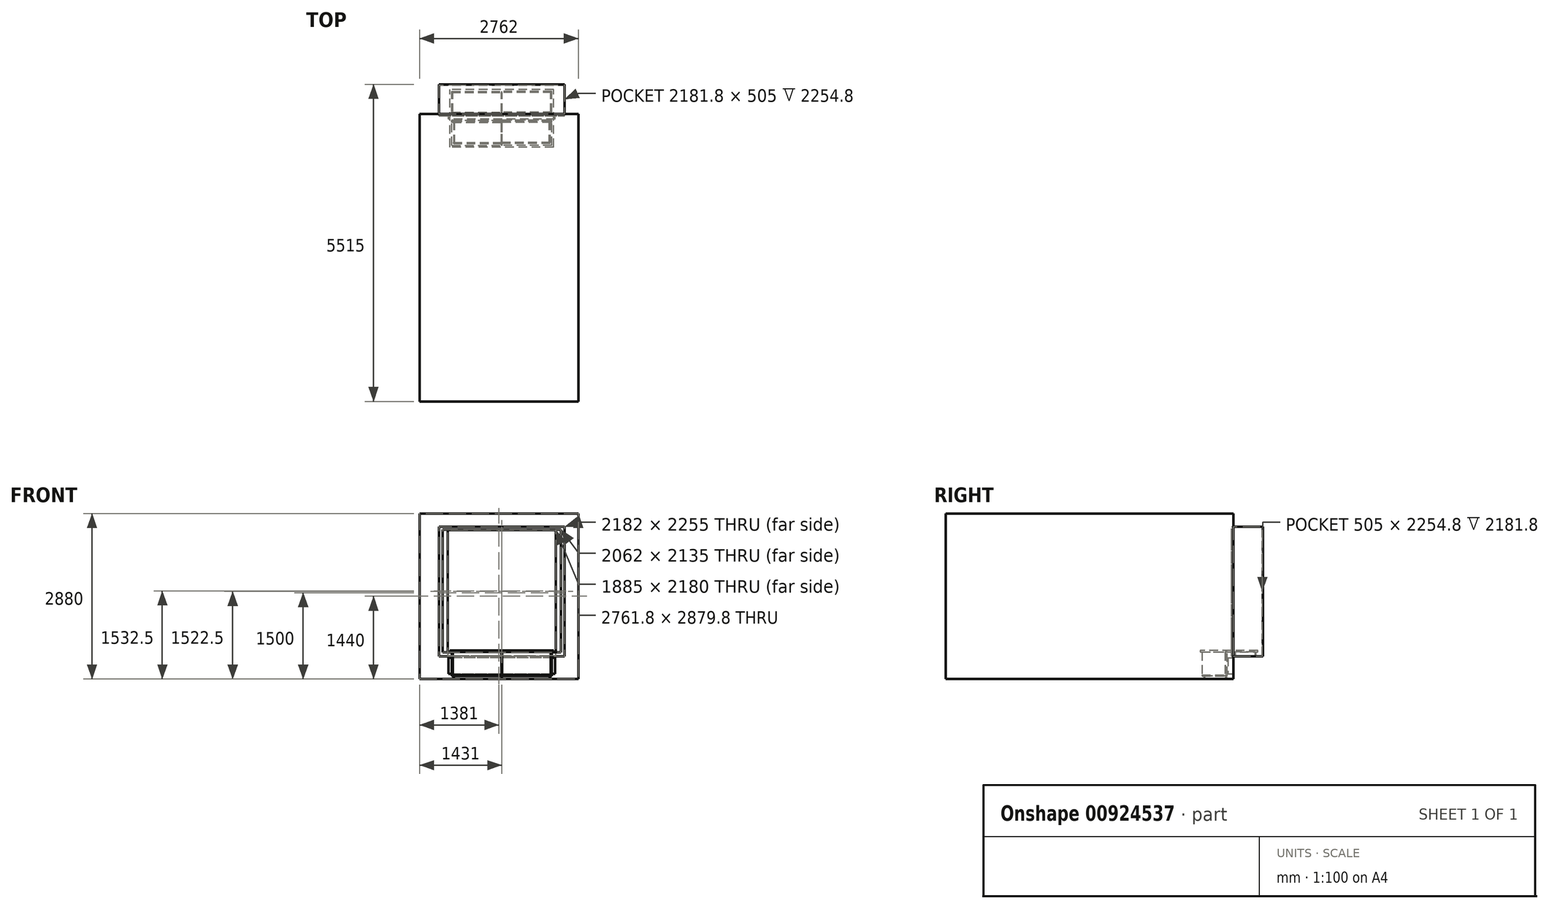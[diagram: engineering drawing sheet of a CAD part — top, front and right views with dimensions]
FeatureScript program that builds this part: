
annotation { "Feature Type Name" : "Feature", "Feature Type Description" : "" }
export const myFeature = defineFeature(function(context is Context, id is Id, definition is map)
    precondition{}
    {
        {
            var Q0;
            Q0=qCreatedBy(makeId("Front.planeOp"),FACE);
            var sketch = newSketch(context, id + "F0", { "sketchPlane" : qUnion([Q0])});
            skLineSegment(sketch, "E0", {"start": v(-1031, 0) * mm, "end": v(1031, 0) * mm});
            skPoint(sketch, "E1", {"position": v(0, 0) * mm});
            skLineSegment(sketch, "E2", {"start": v(-1031, 0) * mm, "end": v(-1031, 2135) * mm});
            skLineSegment(sketch, "E3", {"start": v(-1031, 2135) * mm, "end": v(1031, 2135) * mm});
            skLineSegment(sketch, "E4", {"start": v(1031, 2135) * mm, "end": v(1031, 0) * mm});
            skLineSegment(sketch, "E5", {"start": v(0, 0) * mm, "end": v(0, 2135) * mm, "construction": true});
            skLineSegment(sketch, "E6", {"start": v(-942.5, -55) * mm, "end": v(942.5, -55) * mm, "construction": true});
            skLineSegment(sketch, "E7", {"start": v(942.5, -55) * mm, "end": v(942.5, 2125) * mm, "construction": true});
            skLineSegment(sketch, "E8", {"start": v(942.5, 2125) * mm, "end": v(-942.5, 2125) * mm, "construction": true});
            skLineSegment(sketch, "E9", {"start": v(-942.5, 2125) * mm, "end": v(-942.5, -55) * mm, "construction": true});
            skPoint(sketch, "E10", {"position": v(0, -55) * mm});
            skLineSegment(sketch, "E11.0", {"start": v(-1091, -70) * mm, "end": v(-1091, 2185) * mm});
            skLineSegment(sketch, "E11.1", {"start": v(-1091, -70) * mm, "end": v(1091, -70) * mm});
            skLineSegment(sketch, "E11.2", {"start": v(1091, 2185) * mm, "end": v(1091, -70) * mm});
            skLineSegment(sketch, "E11.3", {"start": v(-1091, 2185) * mm, "end": v(1091, 2185) * mm});
            skPoint(sketch, "E12", {"position": v(0, -70) * mm});
            skLineSegment(sketch, "E13", {"start": v(-1431, -465) * mm, "end": v(-1431, 2415) * mm});
            skLineSegment(sketch, "E14", {"start": v(-1431, 2415) * mm, "end": v(1331, 2415) * mm});
            skLineSegment(sketch, "E15", {"start": v(1331, 2415) * mm, "end": v(1331, -465) * mm});
            skLineSegment(sketch, "E16", {"start": v(1331, -465) * mm, "end": v(-1431, -465) * mm});
            skLineSegment(sketch, "E17.0", {"start": v(-1430.9, -464.9) * mm, "end": v(-1430.9, 2414.9) * mm});
            skLineSegment(sketch, "E17.1", {"start": v(1330.9, -464.9) * mm, "end": v(-1430.9, -464.9) * mm});
            skLineSegment(sketch, "E17.2", {"start": v(1330.9, 2414.9) * mm, "end": v(1330.9, -464.9) * mm});
            skLineSegment(sketch, "E17.3", {"start": v(-1430.9, 2414.9) * mm, "end": v(1330.9, 2414.9) * mm});
            skLineSegment(sketch, "E18.0", {"start": v(-1090.9, -69.9) * mm, "end": v(-1090.9, 2184.9) * mm});
            skLineSegment(sketch, "E18.1", {"start": v(-1090.9, -69.9) * mm, "end": v(1090.9, -69.9) * mm});
            skLineSegment(sketch, "E18.2", {"start": v(1090.9, 2184.9) * mm, "end": v(1090.9, -69.9) * mm});
            skLineSegment(sketch, "E18.3", {"start": v(-1090.9, 2184.9) * mm, "end": v(1090.9, 2184.9) * mm});
            skLineSegment(sketch, "E19", {"start": v(-925, -375) * mm, "end": v(925, -375) * mm});
            skLineSegment(sketch, "E20", {"start": v(925, -375) * mm, "end": v(925, -95) * mm});
            skLineSegment(sketch, "E21", {"start": v(925, -95) * mm, "end": v(-925, -95) * mm});
            skLineSegment(sketch, "E22", {"start": v(-925, -95) * mm, "end": v(-925, -375) * mm});
            skPoint(sketch, "E23", {"position": v(0, -375) * mm});
            skSolve(sketch);
        }
        {
            var Q0;
            Q0=qCreatedBy(makeId("Front.planeOp"),FACE);
            cPlane(context, id + "F1", {"entities" : qUnion([Q0]), "cplaneType" : CPlaneType.OFFSET, "offset" : 515 * mm, "oppositeDirection" : true, "width" : 150 * mm, "height" : 150 * mm});
        }
        {
            var Q0;
            Q0=makeQuery(id+"F0.imprint","IMPRINT",FACE,{"disambiguationData":[TD([[makeQuery(id+"F0.imprint","IMPRINT",EDGE,{"derivedFrom":sQuery(id+"F0.wireOp",EDGE,"E0")}),-1.0]])]});
            extrude(context, id + "F2", {"entities" : qUnion([Q0]), "depth" : 28 * mm, "offsetDistance" : 25 * mm});
        }
        {
            var Q0;
            Q0=qCreatedBy(id+"F1.planeOp",FACE);
            var sketch = newSketch(context, id + "F3", { "sketchPlane" : qUnion([Q0])});
            skLineSegment(sketch, "E24.0", {"start": v(-1091, 2185) * mm, "end": v(1091, 2185) * mm});
            skLineSegment(sketch, "E25.0", {"start": v(-1091, -70) * mm, "end": v(-1091, 2185) * mm});
            skLineSegment(sketch, "E26.0", {"start": v(-1091, -70) * mm, "end": v(1091, -70) * mm});
            skLineSegment(sketch, "E27.0", {"start": v(1091, 2185) * mm, "end": v(1091, -70) * mm});
            skLineSegment(sketch, "E28.0", {"start": v(942.5, 2125) * mm, "end": v(-942.5, 2125) * mm});
            skLineSegment(sketch, "E29.0", {"start": v(-942.5, 2125) * mm, "end": v(-942.5, -55) * mm});
            skLineSegment(sketch, "E30.0", {"start": v(942.5, -55) * mm, "end": v(942.5, 2125) * mm});
            skLineSegment(sketch, "E31.0", {"start": v(-942.5, -55) * mm, "end": v(942.5, -55) * mm});
            skLineSegment(sketch, "E32.0", {"start": v(-1090.9, -69.9) * mm, "end": v(-1090.9, 2184.9) * mm});
            skLineSegment(sketch, "E33.0", {"start": v(-1090.9, 2184.9) * mm, "end": v(1090.9, 2184.9) * mm});
            skLineSegment(sketch, "E34.0", {"start": v(-1090.9, -69.9) * mm, "end": v(1090.9, -69.9) * mm});
            skLineSegment(sketch, "E35.0", {"start": v(1090.9, 2184.9) * mm, "end": v(1090.9, -69.9) * mm});
            skSolve(sketch);
        }
        {
            var Q0;
            Q0=makeQuery(id+"F3.imprint","IMPRINT",FACE,{"disambiguationData":[TD([[makeQuery(id+"F3.imprint","IMPRINT",EDGE,{"derivedFrom":sQuery(id+"F3.wireOp",EDGE,"E24.0")}),-1.0]])]});
            var Q1;
            Q1=makeQuery(id+"F2.opExtrude","CAP_FACE",FACE,{"disambiguationData":[OSD([sQuery(id+"F0.wireOp",EDGE,"E0"),sQuery(id+"F0.wireOp",EDGE,"E2"),sQuery(id+"F0.wireOp",EDGE,"E3"),sQuery(id+"F0.wireOp",EDGE,"E4"),sQuery(id+"F0.wireOp",EDGE,"E18.0"),sQuery(id+"F0.wireOp",EDGE,"E18.1"),sQuery(id+"F0.wireOp",EDGE,"E18.2"),sQuery(id+"F0.wireOp",EDGE,"E18.3")])],"isStart":false});
            extrude(context, id + "F4", {"entities" : qUnion([Q0]), "operationType" : NewBodyOperationType.ADD, "endBound" : BoundingType.UP_TO_SURFACE, "depth" : 25 * mm, "endBoundEntityFace" : qUnion([Q1]), "offsetDistance" : 25 * mm});
        }
        {
            var Q0;
            Q0=makeQuery(id+"F3.imprint","IMPRINT",FACE,{"disambiguationData":[TD([[makeQuery(id+"F3.imprint","IMPRINT",EDGE,{"derivedFrom":sQuery(id+"F3.wireOp",EDGE,"E24.0")}),-1.0]])]});
            var Q1;
            Q1=makeQuery(id+"F3.imprint","IMPRINT",FACE,{"disambiguationData":[TD([[makeQuery(id+"F3.imprint","IMPRINT",EDGE,{"derivedFrom":sQuery(id+"F3.wireOp",EDGE,"E28.0")}),-1.0]])]});
            extrude(context, id + "F5", {"entities" : qUnion([Q0, Q1]), "operationType" : NewBodyOperationType.ADD, "depth" : 10 * mm, "offsetDistance" : 25 * mm});
        }
        {
            var Q0;
            Q0=makeQuery(id+"F0.imprint","IMPRINT",FACE,{"disambiguationData":[TD([[makeQuery(id+"F0.imprint","IMPRINT",EDGE,{"derivedFrom":sQuery(id+"F0.wireOp",EDGE,"E11.0")}),1.0]])]});
            var Q1;
            Q1=makeQuery(id+"F0.imprint","IMPRINT",FACE,{"disambiguationData":[TD([[makeQuery(id+"F0.imprint","IMPRINT",EDGE,{"derivedFrom":sQuery(id+"F0.wireOp",EDGE,"E19")}),1.0]])]});
            extrude(context, id + "F6", {"entities" : qUnion([Q0, Q1]), "operationType" : NewBodyOperationType.ADD, "depth" : .1 * mm, "offsetDistance" : 25 * mm});
        }
        {
            var Q0;
            Q0=makeQuery(id+"F0.imprint","IMPRINT",FACE,{"disambiguationData":[TD([[makeQuery(id+"F0.imprint","IMPRINT",EDGE,{"derivedFrom":sQuery(id+"F0.wireOp",EDGE,"E13")}),-1.0]])]});
            extrude(context, id + "F7", {"entities" : qUnion([Q0]), "depth" : 5000 * mm, "offsetDistance" : 25 * mm});
        }
        {
            var Q0;
            Q0=makeQuery(id+"F6.opExtrude","CAP_FACE",FACE,{"disambiguationData":[OSD([sQuery(id+"F0.wireOp",EDGE,"E11.0"),sQuery(id+"F0.wireOp",EDGE,"E11.1"),sQuery(id+"F0.wireOp",EDGE,"E11.2"),sQuery(id+"F0.wireOp",EDGE,"E11.3"),sQuery(id+"F0.wireOp",EDGE,"E17.0"),sQuery(id+"F0.wireOp",EDGE,"E17.1"),sQuery(id+"F0.wireOp",EDGE,"E17.2"),sQuery(id+"F0.wireOp",EDGE,"E17.3")])],"isStart":false});
            var sketch = newSketch(context, id + "F8", { "sketchPlane" : qUnion([Q0])});
            skLineSegment(sketch, "E36.0", {"start": v(-925, -95) * mm, "end": v(-925, -375) * mm});
            skLineSegment(sketch, "E37.0", {"start": v(925, -95) * mm, "end": v(-925, -95) * mm});
            skLineSegment(sketch, "E38.0", {"start": v(-925, -375) * mm, "end": v(925, -375) * mm});
            skLineSegment(sketch, "E39.0", {"start": v(925, -375) * mm, "end": v(925, -95) * mm});
            skSolve(sketch);
        }
        {
            var Q0;
            Q0=makeQuery(id+"F8.imprint","IMPRINT",FACE,{"disambiguationData":[TD([[makeQuery(id+"F8.imprint","IMPRINT",EDGE,{"derivedFrom":sQuery(id+"F8.wireOp",EDGE,"E36.0")}),1.0]])]});
            extrude(context, id + "F9", {"entities" : qUnion([Q0]), "operationType" : NewBodyOperationType.ADD, "depth" : 90 * mm, "offsetDistance" : 25 * mm});
        }
        {
            var Q0;
            Q0=qCreatedBy(makeId("Right.planeOp"),FACE);
            var sketch = newSketch(context, id + "F10", { "sketchPlane" : qUnion([Q0])});
            skLineSegment(sketch, "E40.0", {"start": v(-5000, -465) * mm, "end": v(0, -465) * mm, "construction": true});
            skLineSegment(sketch, "E41.0", {"start": v(0, 2415) * mm, "end": v(0, -465) * mm, "construction": true});
            skLineSegment(sketch, "E42.0", {"start": v(-90.1, -375) * mm, "end": v(-0.1, -375) * mm, "construction": true});
            skLineSegment(sketch, "E43.0", {"start": v(-90.1, -375) * mm, "end": v(-90.1, -95) * mm, "construction": true});
            skLineSegment(sketch, "E44.0", {"start": v(-90.1, -95) * mm, "end": v(-0.1, -95) * mm, "construction": true});
            skLineSegment(sketch, "E45.0", {"start": v(-28, 2185) * mm, "end": v(-28, -70) * mm, "construction": true});
            skLineSegment(sketch, "E46.0", {"start": v(0, -70) * mm, "end": v(515, -70) * mm, "construction": true});
            skLineSegment(sketch, "E47.0", {"start": v(515, 2185) * mm, "end": v(515, -70) * mm, "construction": true});
            skLineSegment(sketch, "E48.0", {"start": v(-28, -70) * mm, "end": v(-0.1, -70) * mm, "construction": true});
            skLineSegment(sketch, "E49.0", {"start": v(-28, 0) * mm, "end": v(0, 0) * mm, "construction": true});
            skLineSegment(sketch, "E50.0", {"start": v(505, -69.9) * mm, "end": v(505, 2184.9) * mm, "construction": true});
            skLineSegment(sketch, "E51.0", {"start": v(505, -55) * mm, "end": v(515, -55) * mm, "construction": true});
            skLineSegment(sketch, "E52", {"start": v(-575, 5) * mm, "end": v(425, 5) * mm});
            skLineSegment(sketch, "E53", {"start": v(425, 5) * mm, "end": v(425, 33) * mm});
            skLineSegment(sketch, "E54", {"start": v(425, 33) * mm, "end": v(-575, 33) * mm});
            skLineSegment(sketch, "E55", {"start": v(-575, 33) * mm, "end": v(-575, 5) * mm});
            skLineSegment(sketch, "E56", {"start": v(-545, 5) * mm, "end": v(-545, -415) * mm});
            skLineSegment(sketch, "E57", {"start": v(-545, -415) * mm, "end": v(-105.1, -415) * mm});
            skLineSegment(sketch, "E58", {"start": v(-105.1, -415) * mm, "end": v(-105.1, 5) * mm});
            skLineSegment(sketch, "E59", {"start": v(-515, -415) * mm, "end": v(-515, -465) * mm});
            skLineSegment(sketch, "E60", {"start": v(-515, -465) * mm, "end": v(-110.1, -465) * mm});
            skLineSegment(sketch, "E61", {"start": v(-110.1, -465) * mm, "end": v(-110.1, -415) * mm});
            skLineSegment(sketch, "E62", {"start": v(15, 5) * mm, "end": v(15, -70) * mm});
            skLineSegment(sketch, "E63", {"start": v(15, -70) * mm, "end": v(395, -70) * mm});
            skLineSegment(sketch, "E64", {"start": v(395, -70) * mm, "end": v(395, 5) * mm});
            skLineSegment(sketch, "E65", {"start": v(-545, -397) * mm, "end": v(-105.1, -397) * mm});
            skLineSegment(sketch, "E66", {"start": v(-145, 5) * mm, "end": v(-145, -397) * mm});
            skLineSegment(sketch, "E67", {"start": v(-139, 5) * mm, "end": v(-139, -397) * mm});
            skLineSegment(sketch, "E68", {"start": v(-90.1, -164.5) * mm, "end": v(-125.1, -164.5) * mm, "construction": true});
            skLineSegment(sketch, "E69", {"start": v(-125.1, -164.5) * mm, "end": v(-125.1, -293.45) * mm, "construction": true});
            skLineSegment(sketch, "E70", {"start": v(-125.1, -293.45) * mm, "end": v(-90.1, -293.45) * mm, "construction": true});
            skLineSegment(sketch, "E71", {"start": v(-497, -415) * mm, "end": v(-497, -465) * mm});
            skLineSegment(sketch, "E72", {"start": v(-128.1, -415) * mm, "end": v(-128.1, -465) * mm});
            skLineSegment(sketch, "E73", {"start": v(377, 5) * mm, "end": v(377, -70) * mm});
            skLineSegment(sketch, "E74", {"start": v(33, 5) * mm, "end": v(33, -70) * mm});
            skSolve(sketch);
        }
        {
            var Q0;
            {var subQ0=sQuery(id+"F10.wireOp",EDGE,"E53");Q0=makeQuery(id+"F10.imprint","IMPRINT",FACE,{"disambiguationData":[TD([[makeQuery(id+"F10.imprint","IMPRINT",EDGE,{"derivedFrom":subQ0}),1.0]])]});}
            extrude(context, id + "F11", {"entities" : qUnion([Q0]), "depth" : 1800 * mm, "offsetDistance" : 25 * mm, "symmetric" : true});
        }
        {
            var Q0;
            Q0=makeQuery(id+"F11.opExtrude","CAP_FACE",FACE,{"disambiguationData":[OSD([sQuery(id+"F10.wireOp",EDGE,"E52"),sQuery(id+"F10.wireOp",EDGE,"E53"),sQuery(id+"F10.wireOp",EDGE,"E54"),sQuery(id+"F10.wireOp",EDGE,"E55")])],"isStart":false});
            cPlane(context, id + "F12", {"entities" : qUnion([Q0]), "cplaneType" : CPlaneType.OFFSET, "offset" : 30 * mm, "oppositeDirection" : true, "width" : 150 * mm, "height" : 150 * mm});
        }
        {
            var Q0;
            {var subQ0=sQuery(id+"F10.wireOp",EDGE,"E57");var subQ4=sQuery(id+"F10.wireOp",EDGE,"E56");var subQ5=makeQuery(id+"F10.imprint","INTERSECT",VERTEX,{"derivedFrom":[subQ4,subQ0]});Q0=makeQuery(id+"F10.imprint","IMPRINT",FACE,{"disambiguationData":[TD([[makeQuery(id+"F10.imprint","IMPRINT",EDGE,{"disambiguationData":[TD([[subQ5,1.0]])],"derivedFrom":subQ4}),1.0]])]});}
            var Q1;
            {var subQ0=sQuery(id+"F10.wireOp",EDGE,"E62");Q1=makeQuery(id+"F10.imprint","IMPRINT",FACE,{"disambiguationData":[TD([[makeQuery(id+"F10.imprint","IMPRINT",EDGE,{"derivedFrom":subQ0}),1.0]])]});}
            var Q2;
            {var subQ0=sQuery(id+"F10.wireOp",EDGE,"E64");Q2=makeQuery(id+"F10.imprint","IMPRINT",FACE,{"disambiguationData":[TD([[makeQuery(id+"F10.imprint","IMPRINT",EDGE,{"derivedFrom":subQ0}),1.0]])]});}
            var Q3;
            Q3=qCreatedBy(id+"F12.planeOp",FACE);
            extrude(context, id + "F13", {"entities" : qUnion([Q0, Q1, Q2]), "endBound" : BoundingType.UP_TO_SURFACE, "depth" : 25 * mm, "endBoundEntityFace" : qUnion([Q3]), "offsetDistance" : 25 * mm});
        }
        {
            var Q0;
            Q0=makeQuery(id+"F13.opExtrude","CAP_FACE",FACE,{"disambiguationData":[OSD([sQuery(id+"F10.wireOp",EDGE,"E56"),sQuery(id+"F10.wireOp",EDGE,"E57"),sQuery(id+"F10.wireOp",EDGE,"E58"),sQuery(id+"F10.wireOp",EDGE,"E65")])],"isStart":false});
            cPlane(context, id + "F14", {"entities" : qUnion([Q0]), "cplaneType" : CPlaneType.OFFSET, "offset" : 30 * mm, "oppositeDirection" : true, "width" : 150 * mm, "height" : 150 * mm});
        }
        {
            var Q0;
            {var subQ0=sQuery(id+"F10.wireOp",EDGE,"E59");Q0=makeQuery(id+"F10.imprint","IMPRINT",FACE,{"disambiguationData":[TD([[makeQuery(id+"F10.imprint","IMPRINT",EDGE,{"derivedFrom":subQ0}),1.0]])]});}
            var Q1;
            {var subQ0=sQuery(id+"F10.wireOp",EDGE,"E61");Q1=makeQuery(id+"F10.imprint","IMPRINT",FACE,{"disambiguationData":[TD([[makeQuery(id+"F10.imprint","IMPRINT",EDGE,{"derivedFrom":subQ0}),1.0]])]});}
            var Q2;
            Q2=qCreatedBy(id+"F14.planeOp",FACE);
            extrude(context, id + "F15", {"entities" : qUnion([Q0, Q1]), "endBound" : BoundingType.UP_TO_SURFACE, "depth" : 25 * mm, "endBoundEntityFace" : qUnion([Q2]), "offsetDistance" : 25 * mm});
        }
        {
            var Q0;
            Q0=qCreatedBy(id+"F12.planeOp",FACE);
            var sketch = newSketch(context, id + "F16", { "sketchPlane" : qUnion([Q0])});
            skLineSegment(sketch, "E75.0.0", {"start": v(377, -70) * mm, "end": v(377, 5) * mm});
            skLineSegment(sketch, "E75.0.1", {"start": v(377, 5) * mm, "end": v(33, 5) * mm});
            skLineSegment(sketch, "E75.0.2", {"start": v(33, 5) * mm, "end": v(33, -70) * mm});
            skLineSegment(sketch, "E75.0.3", {"start": v(33, -70) * mm, "end": v(377, -70) * mm});
            skLineSegment(sketch, "E76.0.0", {"start": v(-139, -397) * mm, "end": v(-139, 5) * mm});
            skLineSegment(sketch, "E76.0.1", {"start": v(-139, 5) * mm, "end": v(-145, 5) * mm});
            skLineSegment(sketch, "E76.0.2", {"start": v(-145, 5) * mm, "end": v(-145, -397) * mm});
            skLineSegment(sketch, "E76.0.3", {"start": v(-145, -397) * mm, "end": v(-139, -397) * mm});
            skLineSegment(sketch, "E77.0.0", {"start": v(-145, -397) * mm, "end": v(-145, 5) * mm});
            skLineSegment(sketch, "E77.0.1", {"start": v(-145, 5) * mm, "end": v(-545, 5) * mm});
            skLineSegment(sketch, "E77.0.2", {"start": v(-545, 5) * mm, "end": v(-545, -397) * mm});
            skLineSegment(sketch, "E77.0.3", {"start": v(-545, -397) * mm, "end": v(-145, -397) * mm});
            skLineSegment(sketch, "E78.0.0", {"start": v(-105.1, 5) * mm, "end": v(-139, 5) * mm});
            skLineSegment(sketch, "E78.0.1", {"start": v(-139, 5) * mm, "end": v(-139, -397) * mm});
            skLineSegment(sketch, "E78.0.2", {"start": v(-139, -397) * mm, "end": v(-105.1, -397) * mm});
            skLineSegment(sketch, "E78.0.3", {"start": v(-105.1, -397) * mm, "end": v(-105.1, 5) * mm});
            skSolve(sketch);
        }
        {
            var Q0;
            Q0=makeQuery(id+"F16.imprint","IMPRINT",FACE,{"disambiguationData":[TD([[makeQuery(id+"F16.imprint","IMPRINT",EDGE,{"derivedFrom":sQuery(id+"F16.wireOp",EDGE,"E75.0.0")}),1.0]])]});
            var Q1;
            Q1=makeQuery(id+"F16.imprint","IMPRINT",FACE,{"disambiguationData":[TD([[makeQuery(id+"F16.imprint","IMPRINT",EDGE,{"derivedFrom":sQuery(id+"F16.wireOp",EDGE,"E77.0.0")}),1.0]])]});
            var Q2;
            Q2=makeQuery(id+"F16.imprint","IMPRINT",FACE,{"disambiguationData":[TD([[makeQuery(id+"F16.imprint","IMPRINT",EDGE,{"derivedFrom":sQuery(id+"F16.wireOp",EDGE,"E76.0.1")}),1.0]])]});
            var Q3;
            Q3=makeQuery(id+"F16.imprint","IMPRINT",FACE,{"disambiguationData":[TD([[makeQuery(id+"F16.imprint","IMPRINT",EDGE,{"derivedFrom":sQuery(id+"F16.wireOp",EDGE,"E78.0.0")}),1.0]])]});
            extrude(context, id + "F17", {"entities" : qUnion([Q0, Q1, Q2, Q3]), "oppositeDirection" : true, "depth" : 18 * mm, "offsetDistance" : 25 * mm});
        }
        {
            var Q0;
            Q0=qCreatedBy(id+"F14.planeOp",FACE);
            var sketch = newSketch(context, id + "F18", { "sketchPlane" : qUnion([Q0])});
            skLineSegment(sketch, "E79.0.0", {"start": v(-497, -415) * mm, "end": v(-497, -465) * mm});
            skLineSegment(sketch, "E79.0.1", {"start": v(-497, -465) * mm, "end": v(-128.1, -465) * mm});
            skLineSegment(sketch, "E79.0.2", {"start": v(-128.1, -465) * mm, "end": v(-128.1, -415) * mm});
            skLineSegment(sketch, "E79.0.3", {"start": v(-128.1, -415) * mm, "end": v(-497, -415) * mm});
            skSolve(sketch);
        }
        {
            var Q0;
            Q0=makeQuery(id+"F18.imprint","IMPRINT",FACE,{"disambiguationData":[TD([[makeQuery(id+"F18.imprint","IMPRINT",EDGE,{"derivedFrom":sQuery(id+"F18.wireOp",EDGE,"E79.0.0")}),1.0]])]});
            extrude(context, id + "F19", {"entities" : qUnion([Q0]), "oppositeDirection" : true, "depth" : 18 * mm, "offsetDistance" : 25 * mm});
        }
        {
            var Q0;
            {var subQ3=sQuery(id+"F10.wireOp",EDGE,"E66");Q0=makeQuery(id+"F10.imprint","IMPRINT",FACE,{"disambiguationData":[TD([[makeQuery(id+"F10.imprint","IMPRINT",EDGE,{"derivedFrom":subQ3}),-1.0]])]});}
            var Q1;
            {var subQ0=sQuery(id+"F10.wireOp",EDGE,"E71");Q1=makeQuery(id+"F10.imprint","IMPRINT",FACE,{"disambiguationData":[TD([[makeQuery(id+"F10.imprint","IMPRINT",EDGE,{"derivedFrom":subQ0}),1.0]])]});}
            var Q2;
            {var subQ0=sQuery(id+"F10.wireOp",EDGE,"E73");Q2=makeQuery(id+"F10.imprint","IMPRINT",FACE,{"disambiguationData":[TD([[makeQuery(id+"F10.imprint","IMPRINT",EDGE,{"derivedFrom":subQ0}),-1.0]])]});}
            extrude(context, id + "F20", {"entities" : qUnion([Q0, Q1, Q2]), "depth" : 18 * mm, "offsetDistance" : 25 * mm, "symmetric" : true});
        }
        {
            var Q0;
            {var subQ0=sQuery(id+"F10.wireOp",EDGE,"E66");Q0=makeQuery(id+"F10.imprint","IMPRINT",FACE,{"disambiguationData":[TD([[makeQuery(id+"F10.imprint","IMPRINT",EDGE,{"derivedFrom":subQ0}),1.0]])]});}
            var Q1;
            Q1=makeQuery(id+"F17.opExtrude","CAP_FACE",FACE,{"disambiguationData":[OSD([sQuery(id+"F16.wireOp",EDGE,"E76.0.1"),sQuery(id+"F16.wireOp",EDGE,"E76.0.3"),sQuery(id+"F16.wireOp",EDGE,"E77.0.1"),sQuery(id+"F16.wireOp",EDGE,"E77.0.2"),sQuery(id+"F16.wireOp",EDGE,"E77.0.3"),sQuery(id+"F16.wireOp",EDGE,"E78.0.0"),sQuery(id+"F16.wireOp",EDGE,"E78.0.2"),sQuery(id+"F16.wireOp",EDGE,"E78.0.3")])],"isStart":false});
            extrude(context, id + "F21", {"entities" : qUnion([Q0]), "endBound" : BoundingType.UP_TO_SURFACE, "depth" : 25 * mm, "endBoundEntityFace" : qUnion([Q1]), "offsetDistance" : 25 * mm});
        }
        {
            var Q0;
            Q0=makeQuery(id+"F15.opExtrude","SWEPT_BODY",BODY,{"disambiguationData":[OSD([sQuery(id+"F10.wireOp",EDGE,"E57"),sQuery(id+"F10.wireOp",EDGE,"E59"),sQuery(id+"F10.wireOp",EDGE,"E60"),sQuery(id+"F10.wireOp",EDGE,"E71")])]});
            var Q1;
            Q1=makeQuery(id+"F15.opExtrude","SWEPT_BODY",BODY,{"disambiguationData":[OSD([sQuery(id+"F10.wireOp",EDGE,"E57"),sQuery(id+"F10.wireOp",EDGE,"E60"),sQuery(id+"F10.wireOp",EDGE,"E61"),sQuery(id+"F10.wireOp",EDGE,"E72")])]});
            var Q2;
            Q2=makeQuery(id+"F13.opExtrude","SWEPT_BODY",BODY,{"disambiguationData":[OSD([sQuery(id+"F10.wireOp",EDGE,"E56"),sQuery(id+"F10.wireOp",EDGE,"E57"),sQuery(id+"F10.wireOp",EDGE,"E58"),sQuery(id+"F10.wireOp",EDGE,"E65")])]});
            var Q3;
            Q3=makeQuery(id+"F21.opExtrude","SWEPT_BODY",BODY,{"disambiguationData":[OSD([sQuery(id+"F10.wireOp",EDGE,"E52"),sQuery(id+"F10.wireOp",EDGE,"E65"),sQuery(id+"F10.wireOp",EDGE,"E66"),sQuery(id+"F10.wireOp",EDGE,"E67")])]});
            var Q4;
            Q4=makeQuery(id+"F17.opExtrude","SWEPT_BODY",BODY,{"disambiguationData":[OSD([sQuery(id+"F16.wireOp",EDGE,"E76.0.1"),sQuery(id+"F16.wireOp",EDGE,"E76.0.3"),sQuery(id+"F16.wireOp",EDGE,"E77.0.1"),sQuery(id+"F16.wireOp",EDGE,"E77.0.2"),sQuery(id+"F16.wireOp",EDGE,"E77.0.3"),sQuery(id+"F16.wireOp",EDGE,"E78.0.0"),sQuery(id+"F16.wireOp",EDGE,"E78.0.2"),sQuery(id+"F16.wireOp",EDGE,"E78.0.3")])]});
            var Q5;
            Q5=makeQuery(id+"F13.opExtrude","SWEPT_BODY",BODY,{"disambiguationData":[OSD([sQuery(id+"F10.wireOp",EDGE,"E52"),sQuery(id+"F10.wireOp",EDGE,"E62"),sQuery(id+"F10.wireOp",EDGE,"E63"),sQuery(id+"F10.wireOp",EDGE,"E74")])]});
            var Q6;
            Q6=makeQuery(id+"F17.opExtrude","SWEPT_BODY",BODY,{"disambiguationData":[OSD([sQuery(id+"F16.wireOp",EDGE,"E75.0.0"),sQuery(id+"F16.wireOp",EDGE,"E75.0.1"),sQuery(id+"F16.wireOp",EDGE,"E75.0.2"),sQuery(id+"F16.wireOp",EDGE,"E75.0.3")])]});
            var Q7;
            Q7=makeQuery(id+"F13.opExtrude","SWEPT_BODY",BODY,{"disambiguationData":[OSD([sQuery(id+"F10.wireOp",EDGE,"E52"),sQuery(id+"F10.wireOp",EDGE,"E63"),sQuery(id+"F10.wireOp",EDGE,"E64"),sQuery(id+"F10.wireOp",EDGE,"E73")])]});
            var Q8;
            Q8=makeQuery(id+"F19.opExtrude","SWEPT_BODY",BODY,{"disambiguationData":[OSD([sQuery(id+"F18.wireOp",EDGE,"E79.0.0"),sQuery(id+"F18.wireOp",EDGE,"E79.0.1"),sQuery(id+"F18.wireOp",EDGE,"E79.0.2"),sQuery(id+"F18.wireOp",EDGE,"E79.0.3")])]});
            var Q9;
            Q9=qCreatedBy(makeId("Right.planeOp"),FACE);
            mirror(context, id + "F22", {"entities" : qUnion([Q0, Q1, Q2, Q3, Q4, Q5, Q6, Q7, Q8]), "mirrorPlane" : qUnion([Q9])});
        }
    });
